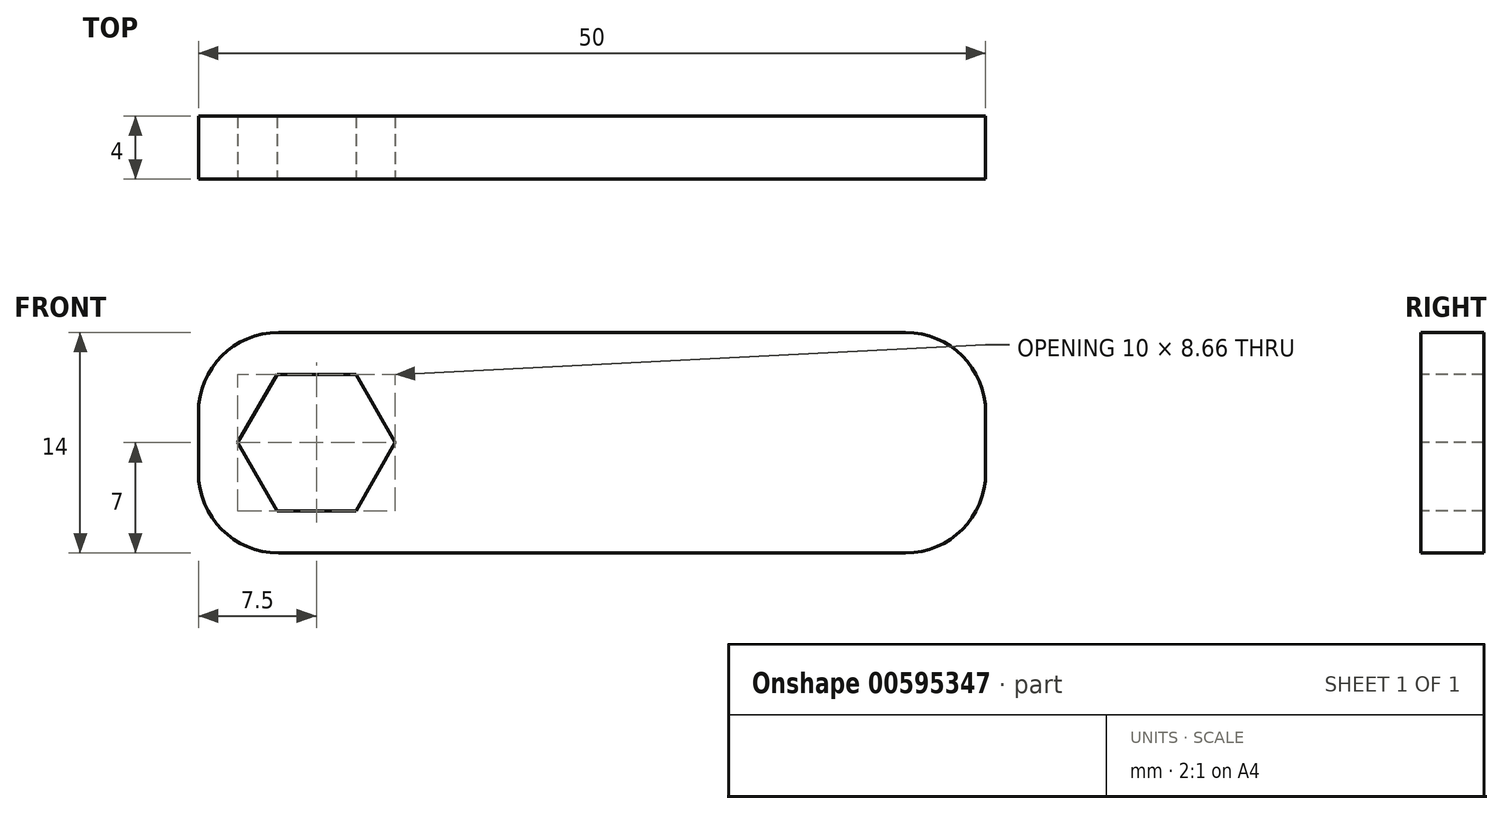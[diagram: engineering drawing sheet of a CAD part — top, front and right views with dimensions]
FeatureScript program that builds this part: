
annotation { "Feature Type Name" : "Feature", "Feature Type Description" : "" }
export const myFeature = defineFeature(function(context is Context, id is Id, definition is map)
    precondition{}
    {
        {
            var Q0;
            Q0=qCreatedBy(makeId("Front.planeOp"),FACE);
            var sketch = newSketch(context, id + "F0", { "sketchPlane" : qUnion([Q0])});
            skLineSegment(sketch, "E0.bottom", {"start": v(0, 0) * mm, "end": v(50, 0) * mm});
            skLineSegment(sketch, "E0.top", {"start": v(0, 14) * mm, "end": v(50, 14) * mm});
            skLineSegment(sketch, "E0.left", {"start": v(0, 0) * mm, "end": v(0, 14) * mm});
            skLineSegment(sketch, "E0.right", {"start": v(50, 0) * mm, "end": v(50, 14) * mm});
            skSolve(sketch);
        }
        {
            var Q0;
            Q0=makeQuery(id+"F0.imprint","IMPRINT",FACE,{"disambiguationData":[TD([[makeQuery(id+"F0.imprint","IMPRINT",EDGE,{"derivedFrom":sQuery(id+"F0.wireOp",EDGE,"E0.bottom")}),1.0]])]});
            extrude(context, id + "F1", {"entities" : qUnion([Q0]), "depth" : 4 * mm, "offsetDistance" : 25.4 * mm});
        }
        {
            var Q0;
            Q0=makeQuery(id+"F1.opExtrude","CAP_FACE",FACE,{"disambiguationData":[OSD([sQuery(id+"F0.wireOp",EDGE,"E0.bottom"),sQuery(id+"F0.wireOp",EDGE,"E0.top"),sQuery(id+"F0.wireOp",EDGE,"E0.left"),sQuery(id+"F0.wireOp",EDGE,"E0.right")])],"isStart":false});
            var sketch = newSketch(context, id + "F2", { "sketchPlane" : qUnion([Q0])});
            skCircle(sketch, "E1.cCircle", {"center": v(7.5, 7) * mm, "radius": 5 * mm, "construction": true});
            skLineSegment(sketch, "E1.0", {"start": v(10, 11.33) * mm, "end": v(12.5, 7) * mm});
            skLineSegment(sketch, "E1.1", {"start": v(12.5, 7) * mm, "end": v(10, 2.67) * mm});
            skLineSegment(sketch, "E1.2", {"start": v(10, 2.67) * mm, "end": v(5, 2.67) * mm});
            skLineSegment(sketch, "E1.3", {"start": v(5, 2.67) * mm, "end": v(2.5, 7) * mm});
            skLineSegment(sketch, "E1.4", {"start": v(2.5, 7) * mm, "end": v(5, 11.33) * mm});
            skLineSegment(sketch, "E1.5", {"start": v(5, 11.33) * mm, "end": v(10, 11.33) * mm});
            skSolve(sketch);
        }
        {
            var Q0;
            Q0 = qSketchRegion(id + "F2", true);
            extrude(context, id + "F3", {"entities" : qUnion([Q0]), "operationType" : NewBodyOperationType.REMOVE, "endBound" : BoundingType.THROUGH_ALL, "oppositeDirection" : true, "depth" : 25.4 * mm, "offsetDistance" : 25.4 * mm});
        }
        {
            var Q0;
            Q0=makeQuery(id+"F1.opExtrude","SWEPT_EDGE",EDGE,{"disambiguationData":[OSD([sQuery(id+"F0.wireOp",EDGE,"E0.top"),sQuery(id+"F0.wireOp",EDGE,"E0.left")])]});
            var Q1;
            Q1=makeQuery(id+"F1.opExtrude","SWEPT_EDGE",EDGE,{"disambiguationData":[OSD([sQuery(id+"F0.wireOp",EDGE,"E0.top"),sQuery(id+"F0.wireOp",EDGE,"E0.right")])]});
            var Q2;
            Q2=makeQuery(id+"F1.opExtrude","SWEPT_EDGE",EDGE,{"disambiguationData":[OSD([sQuery(id+"F0.wireOp",EDGE,"E0.bottom"),sQuery(id+"F0.wireOp",EDGE,"E0.right")])]});
            var Q3;
            Q3=makeQuery(id+"F1.opExtrude","SWEPT_EDGE",EDGE,{"disambiguationData":[OSD([sQuery(id+"F0.wireOp",EDGE,"E0.bottom"),sQuery(id+"F0.wireOp",EDGE,"E0.left")])]});
            fillet(context, id + "F4", {"entities" : qUnion([Q0, Q1, Q2, Q3]), "radius" : 5.08 * mm, "tangentPropagation" : true, "allowEdgeOverflow" : false});
        }
    });
